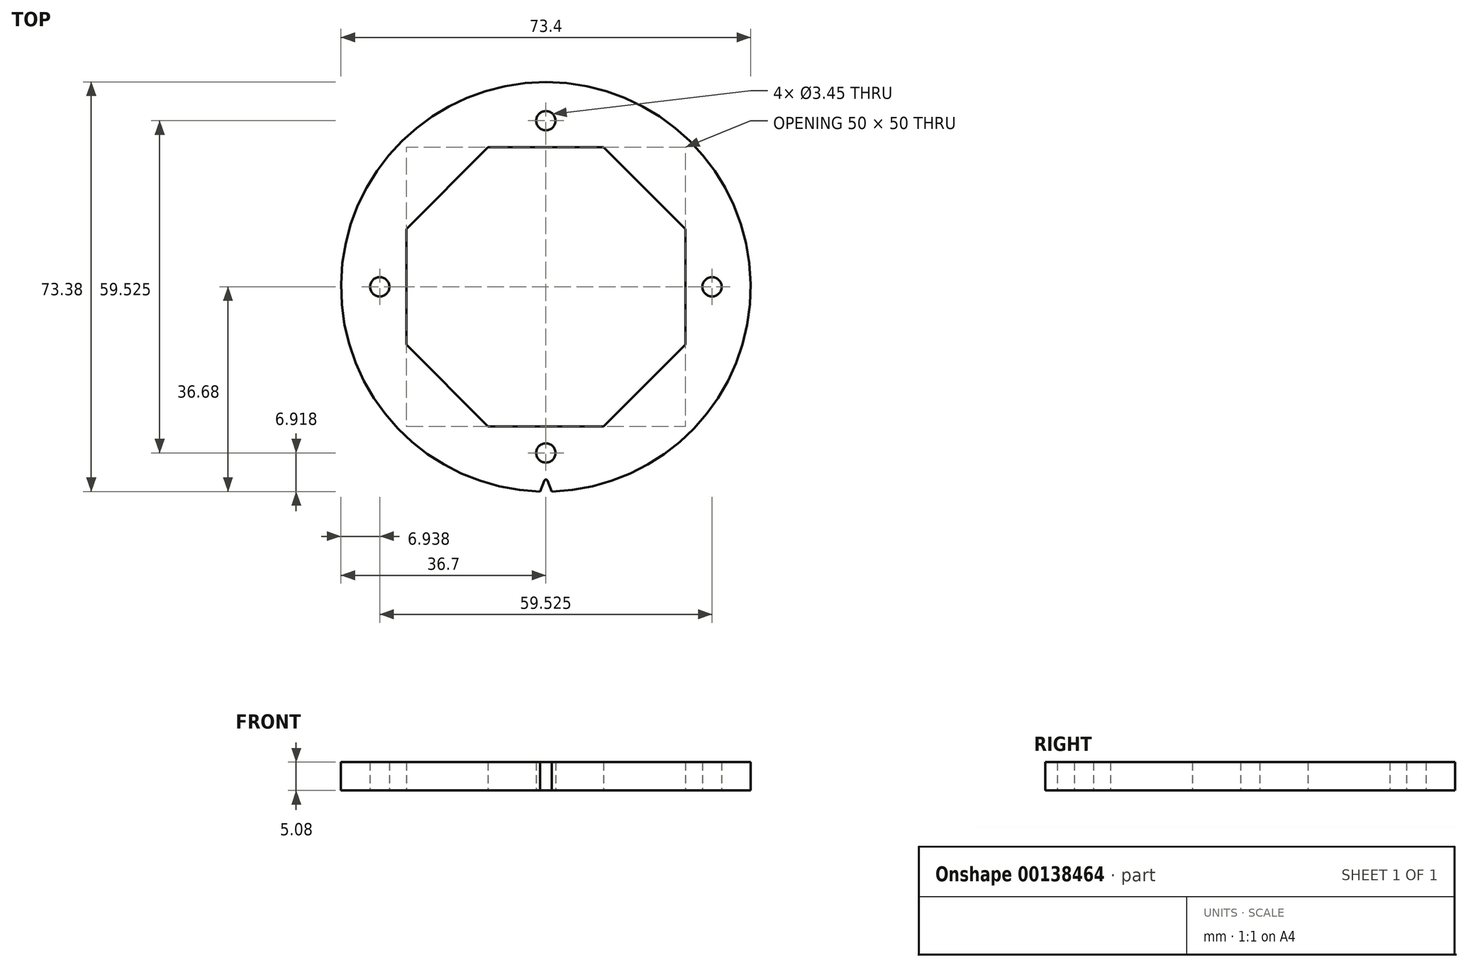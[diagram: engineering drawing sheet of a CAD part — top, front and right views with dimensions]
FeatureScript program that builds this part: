
annotation { "Feature Type Name" : "Feature", "Feature Type Description" : "" }
export const myFeature = defineFeature(function(context is Context, id is Id, definition is map)
    precondition{}
    {
        {
            var Q0;
            Q0=qCreatedBy(makeId("Top.planeOp"),FACE);
            var sketch = newSketch(context, id + "F0", { "sketchPlane" : qUnion([Q0])});
            skCircle(sketch, "E0.cCircle", {"center": v(0, 0) * mm, "radius": 25 * mm, "construction": true});
            skLineSegment(sketch, "E0.0", {"start": v(10.36, -25) * mm, "end": v(-10.36, -25) * mm});
            skLineSegment(sketch, "E0.1", {"start": v(-10.36, -25) * mm, "end": v(-25, -10.36) * mm});
            skLineSegment(sketch, "E0.2", {"start": v(-25, -10.36) * mm, "end": v(-25, 10.36) * mm});
            skLineSegment(sketch, "E0.3", {"start": v(-25, 10.36) * mm, "end": v(-10.36, 25) * mm});
            skLineSegment(sketch, "E0.4", {"start": v(-10.36, 25) * mm, "end": v(10.36, 25) * mm});
            skLineSegment(sketch, "E0.5", {"start": v(10.36, 25) * mm, "end": v(25, 10.36) * mm});
            skLineSegment(sketch, "E0.6", {"start": v(25, 10.36) * mm, "end": v(25, -10.36) * mm});
            skLineSegment(sketch, "E0.7", {"start": v(25, -10.36) * mm, "end": v(10.36, -25) * mm});
            skCircle(sketch, "E1", {"center": v(0, 0) * mm, "radius": 36.7 * mm});
            skPoint(sketch, "E2.centerSnap0", {"position": v(0, 25) * mm});
            skLineSegment(sketch, "E3", {"start": v(0, -29.76) * mm, "end": v(0, 29.76) * mm, "construction": true});
            skLineSegment(sketch, "E4", {"start": v(-29.76, 0) * mm, "end": v(29.76, 0) * mm, "construction": true});
            skCircle(sketch, "E5", {"center": v(0, -29.76) * mm, "radius": 1.73 * mm});
            skCircle(sketch, "E6", {"center": v(29.76, 0) * mm, "radius": 1.73 * mm});
            skCircle(sketch, "E7", {"center": v(0, 29.76) * mm, "radius": 1.73 * mm});
            skCircle(sketch, "E8", {"center": v(-29.76, 0) * mm, "radius": 1.73 * mm});
            skSolve(sketch);
        }
        {
            var Q0;
            Q0=qSketchRegion(id+"F0",true);
            extrude(context, id + "F1", {"entities" : qUnion([Q0]), "depth" : 5.08 * mm});
        }
        {
            var Q0;
            Q0=makeQuery(id+"F1.opExtrude","CAP_FACE",FACE,{"disambiguationData":[OSD([sQuery(id+"F0.wireOp",EDGE,"E0.0"),sQuery(id+"F0.wireOp",EDGE,"E0.1"),sQuery(id+"F0.wireOp",EDGE,"E0.2"),sQuery(id+"F0.wireOp",EDGE,"E0.3"),sQuery(id+"F0.wireOp",EDGE,"E0.4"),sQuery(id+"F0.wireOp",EDGE,"E0.5"),sQuery(id+"F0.wireOp",EDGE,"E0.6"),sQuery(id+"F0.wireOp",EDGE,"E0.7"),sQuery(id+"F0.wireOp",EDGE,"E1"),sQuery(id+"F0.wireOp",EDGE,"E5"),sQuery(id+"F0.wireOp",EDGE,"E6"),sQuery(id+"F0.wireOp",EDGE,"E7"),sQuery(id+"F0.wireOp",EDGE,"E8")])],"isStart":true});
            var sketch = newSketch(context, id + "F2", { "sketchPlane" : qUnion([Q0])});
            skLineSegment(sketch, "E9", {"start": v(0, 0) * mm, "end": v(0, 36.7) * mm, "construction": true});
            skLineSegment(sketch, "E10", {"start": v(0, 0) * mm, "end": v(0.67, 36.7) * mm, "construction": true});
            skArc(sketch, "E11", {"start": v(1.03, 36.68) * mm, "mid": v(0, 36.7) * mm, "end": v(-1.03, 36.68) * mm});
            skLineSegment(sketch, "E12", {"start": v(-1.03, 36.68) * mm, "end": v(-0.28, 34.72) * mm});
            skLineSegment(sketch, "E13", {"start": v(1.03, 36.68) * mm, "end": v(0.28, 34.72) * mm});
            skArc(sketch, "E14", {"start": v(-0.28, 34.72) * mm, "mid": v(0, 34.53) * mm, "end": v(0.28, 34.72) * mm});
            skPoint(sketch, "E15", {"position": v(0.65, 35.7) * mm});
            skSolve(sketch);
        }
        {
            var Q0;
            Q0 = qSketchRegion(id + "F2", true);
            var Q1;
            Q1=makeQuery(id+"F1.opExtrude","CAP_FACE",FACE,{"disambiguationData":[OSD([sQuery(id+"F0.wireOp",EDGE,"E0.0"),sQuery(id+"F0.wireOp",EDGE,"E0.1"),sQuery(id+"F0.wireOp",EDGE,"E0.2"),sQuery(id+"F0.wireOp",EDGE,"E0.3"),sQuery(id+"F0.wireOp",EDGE,"E0.4"),sQuery(id+"F0.wireOp",EDGE,"E0.5"),sQuery(id+"F0.wireOp",EDGE,"E0.6"),sQuery(id+"F0.wireOp",EDGE,"E0.7"),sQuery(id+"F0.wireOp",EDGE,"E1"),sQuery(id+"F0.wireOp",EDGE,"E5"),sQuery(id+"F0.wireOp",EDGE,"E6"),sQuery(id+"F0.wireOp",EDGE,"E7"),sQuery(id+"F0.wireOp",EDGE,"E8")])],"isStart":false});
            extrude(context, id + "F3", {"entities" : qUnion([Q0]), "operationType" : NewBodyOperationType.REMOVE, "endBound" : BoundingType.UP_TO_SURFACE, "oppositeDirection" : true, "endBoundEntityFace" : qUnion([Q1]), "depth" : 25.4 * mm});
        }
    });
